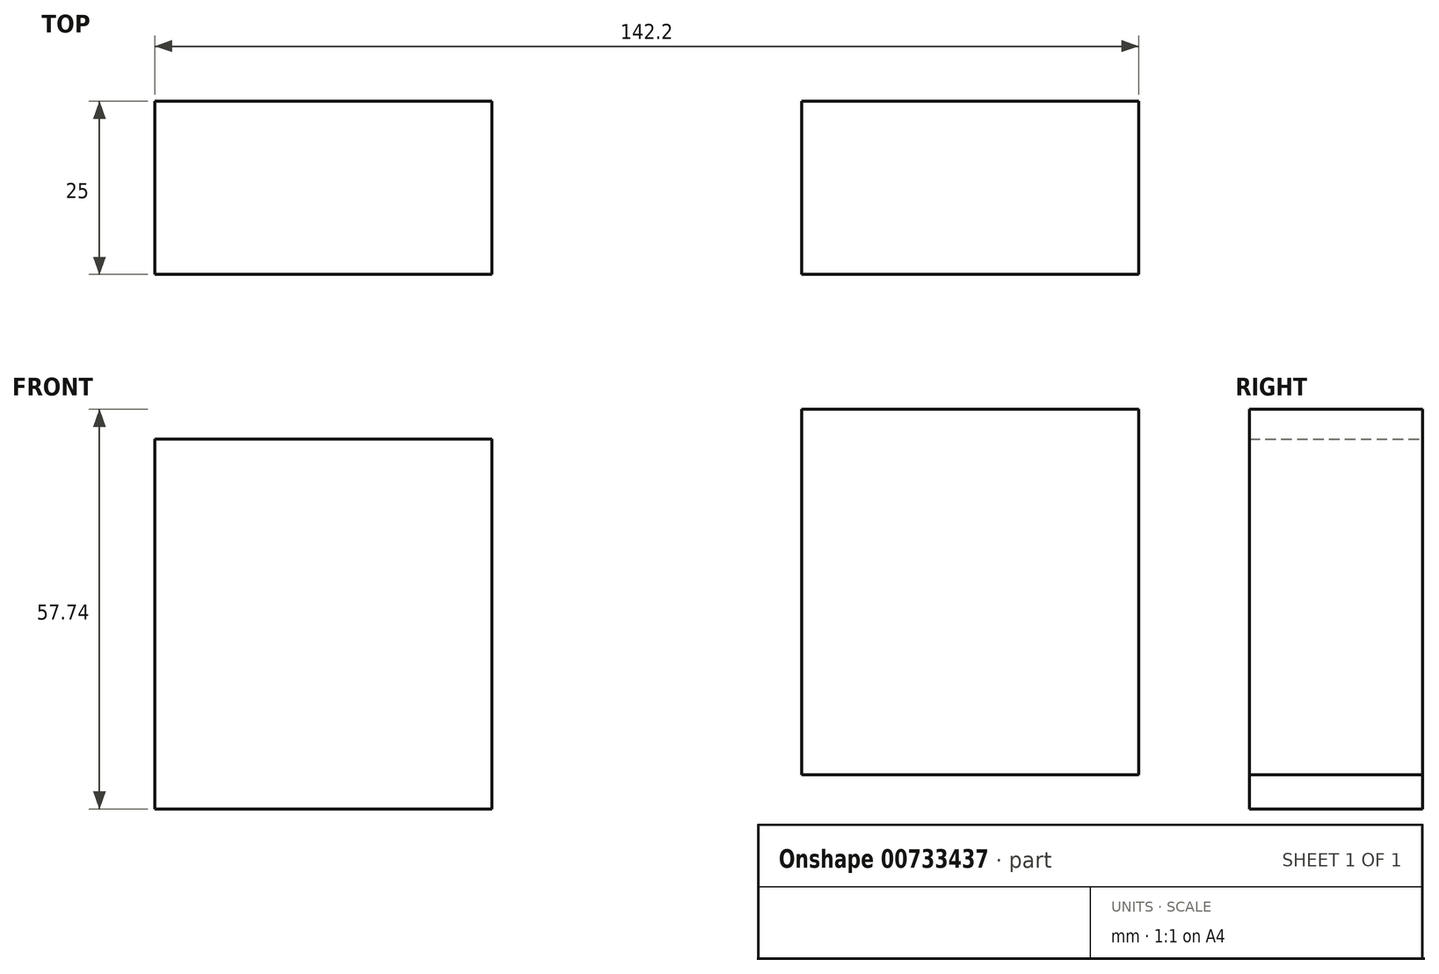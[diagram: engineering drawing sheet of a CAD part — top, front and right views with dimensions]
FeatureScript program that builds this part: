
annotation { "Feature Type Name" : "Feature", "Feature Type Description" : "" }
export const myFeature = defineFeature(function(context is Context, id is Id, definition is map)
    precondition{}
    {
        {
            var Q0;
            Q0=qCreatedBy(makeId("Front.planeOp"),FACE);
            var sketch = newSketch(context, id + "F0", { "sketchPlane" : qUnion([Q0])});
            skLineSegment(sketch, "E0.bottom", {"start": v(-152.7, -11.54) * mm, "end": v(-103.97, -11.54) * mm});
            skLineSegment(sketch, "E0.top", {"start": v(-152.7, 41.92) * mm, "end": v(-103.97, 41.92) * mm});
            skLineSegment(sketch, "E0.left", {"start": v(-152.7, -11.54) * mm, "end": v(-152.7, 41.92) * mm});
            skLineSegment(sketch, "E0.right", {"start": v(-103.97, -11.54) * mm, "end": v(-103.97, 41.92) * mm});
            skPoint(sketch, "E0.middle", {"position": v(-128.34, 15.19) * mm});
            skLineSegment(sketch, "E1.bottom", {"start": v(-59.25, -6.59) * mm, "end": v(-10.51, -6.59) * mm});
            skLineSegment(sketch, "E1.top", {"start": v(-59.25, 46.2) * mm, "end": v(-10.51, 46.2) * mm});
            skLineSegment(sketch, "E1.left", {"start": v(-59.25, -6.59) * mm, "end": v(-59.25, 46.2) * mm});
            skLineSegment(sketch, "E1.right", {"start": v(-10.51, -6.59) * mm, "end": v(-10.51, 46.2) * mm});
            skPoint(sketch, "E1.middle", {"position": v(-34.88, 19.8) * mm});
            skSolve(sketch);
        }
        {
            var Q0;
            Q0=makeQuery(id+"F0.imprint","IMPRINT",FACE,{"disambiguationData":[TD([[makeQuery(id+"F0.imprint","IMPRINT",EDGE,{"derivedFrom":sQuery(id+"F0.wireOp",EDGE,"E0.bottom")}),1.0]])]});
            var Q1;
            Q1=makeQuery(id+"F0.imprint","IMPRINT",FACE,{"disambiguationData":[TD([[makeQuery(id+"F0.imprint","IMPRINT",EDGE,{"derivedFrom":sQuery(id+"F0.wireOp",EDGE,"E1.bottom")}),1.0]])]});
            extrude(context, id + "F1", {"entities" : qUnion([Q0, Q1]), "depth" : 25 * mm, "offsetDistance" : 25 * mm});
        }
    });
